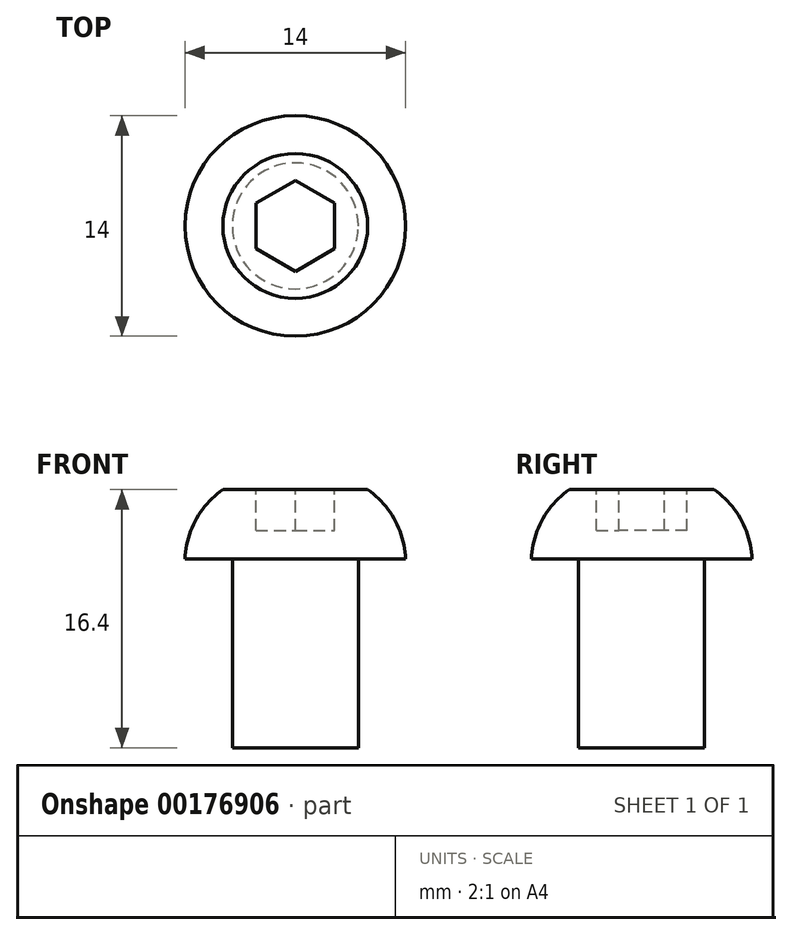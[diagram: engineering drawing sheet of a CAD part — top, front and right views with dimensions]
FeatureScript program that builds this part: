
annotation { "Feature Type Name" : "Feature", "Feature Type Description" : "" }
export const myFeature = defineFeature(function(context is Context, id is Id, definition is map)
    precondition{}
    {
        {
            var Q0;
            Q0=qCreatedBy(makeId("Top.planeOp"),FACE);
            var sketch = newSketch(context, id + "F0", { "sketchPlane" : qUnion([Q0])});
            skCircle(sketch, "E0", {"center": v(0, 0) * mm, "radius": 7 * mm});
            skSolve(sketch);
        }
        {
            var Q0;
            Q0=makeQuery(id+"F0.imprint","IMPRINT",FACE,{"disambiguationData":[TD([[makeQuery(id+"F0.imprint","IMPRINT",EDGE,{"derivedFrom":sQuery(id+"F0.wireOp",EDGE,"E0")}),1.0]])]});
            extrude(context, id + "F1", {"entities" : qUnion([Q0]), "depth" : 4.4 * mm});
        }
        {
            var Q0;
            Q0=makeQuery(id+"F1.opExtrude","CAP_FACE",FACE,{"disambiguationData":[OSD([sQuery(id+"F0.wireOp",EDGE,"E0")])],"isStart":false});
            var sketch = newSketch(context, id + "F2", { "sketchPlane" : qUnion([Q0])});
            skCircle(sketch, "E1.cCircle", {"center": v(0, 0) * mm, "radius": 2.5 * mm, "construction": true});
            skLineSegment(sketch, "E1.0", {"start": v(2.5, 1.44) * mm, "end": v(2.5, -1.44) * mm});
            skLineSegment(sketch, "E1.1", {"start": v(2.5, -1.44) * mm, "end": v(0, -2.89) * mm});
            skLineSegment(sketch, "E1.2", {"start": v(0, -2.89) * mm, "end": v(-2.5, -1.44) * mm});
            skLineSegment(sketch, "E1.3", {"start": v(-2.5, -1.44) * mm, "end": v(-2.5, 1.44) * mm});
            skLineSegment(sketch, "E1.4", {"start": v(-2.5, 1.44) * mm, "end": v(0, 2.89) * mm});
            skLineSegment(sketch, "E1.5", {"start": v(0, 2.89) * mm, "end": v(2.5, 1.44) * mm});
            skPoint(sketch, "E1.0.midPoint", {"position": v(2.5, 0) * mm});
            skSolve(sketch);
        }
        {
            var Q0;
            Q0=makeQuery(id+"F2.imprint","IMPRINT",FACE,{"disambiguationData":[TD([[makeQuery(id+"F2.imprint","IMPRINT",EDGE,{"derivedFrom":sQuery(id+"F2.wireOp",EDGE,"E1.0")}),-1.0]])]});
            extrude(context, id + "F3", {"entities" : qUnion([Q0]), "operationType" : NewBodyOperationType.REMOVE, "oppositeDirection" : true, "depth" : 2.6 * mm});
        }
        {
            var Q0;
            Q0=qCreatedBy(makeId("Right.planeOp"),FACE);
            var sketch = newSketch(context, id + "F4", { "sketchPlane" : qUnion([Q0])});
            skLineSegment(sketch, "E2.0", {"start": v(-7, 0) * mm, "end": v(7, 0) * mm});
            skLineSegment(sketch, "E3", {"start": v(-7, 0) * mm, "end": v(-7, 4.4) * mm});
            skLineSegment(sketch, "E4.0", {"start": v(-7, 4.4) * mm, "end": v(7, 4.4) * mm});
            skArc(sketch, "E5", {"start": v(-4.6, 4.4) * mm, "mid": v(-6.32, 2.48) * mm, "end": v(-7, 0) * mm});
            skLineSegment(sketch, "E6", {"start": v(0, 0) * mm, "end": v(0, 4.4) * mm, "construction": true});
            skSolve(sketch);
        }
        {
            var Q0;
            Q0 = qSketchRegion(id + "F4", true);
            var Q1;
            Q1=sQuery(id+"F4.wireOp",EDGE,"E6");
            revolve(context, id + "F5", {"operationType" : NewBodyOperationType.REMOVE, "entities" : qUnion([Q0]), "axis" : qUnion([Q1]), "revolveType" : RevolveType.FULL, "oppositeDirection" : true});
        }
        {
            var Q0;
            Q0=qCreatedBy(makeId("Top.planeOp"),FACE);
            var sketch = newSketch(context, id + "F6", { "sketchPlane" : qUnion([Q0])});
            skCircle(sketch, "E7", {"center": v(0, 0) * mm, "radius": 4 * mm});
            skSolve(sketch);
        }
        {
            var Q0;
            Q0=makeQuery(id+"F6.imprint","IMPRINT",FACE,{"disambiguationData":[TD([[makeQuery(id+"F6.imprint","IMPRINT",EDGE,{"derivedFrom":sQuery(id+"F6.wireOp",EDGE,"E7")}),1.0]])]});
            extrude(context, id + "F7", {"entities" : qUnion([Q0]), "operationType" : NewBodyOperationType.ADD, "oppositeDirection" : true, "depth" : 12 * mm});
        }
    });
